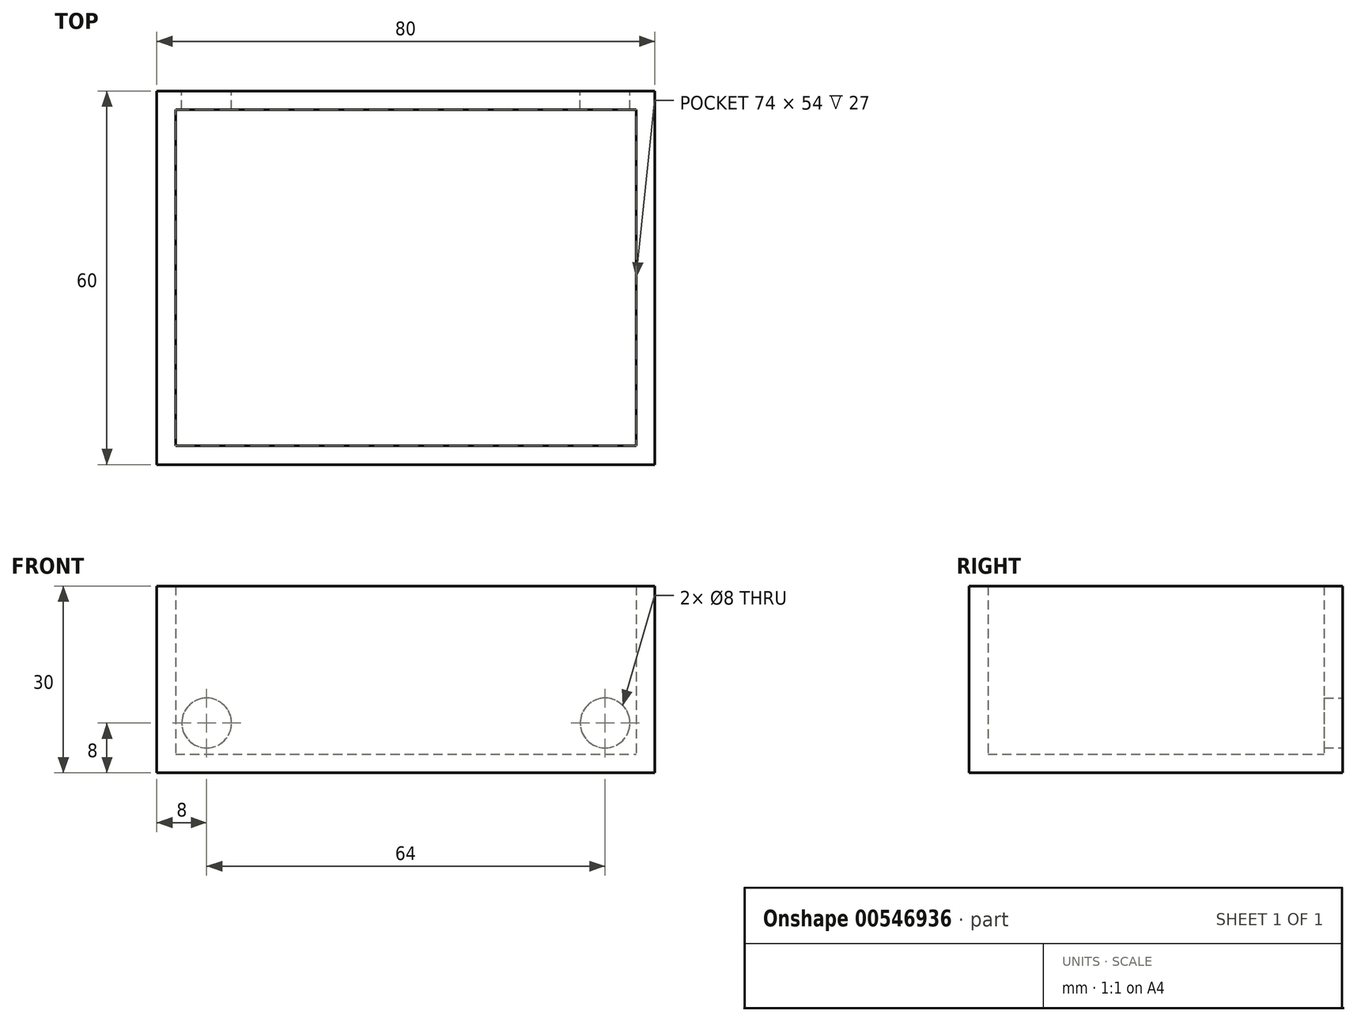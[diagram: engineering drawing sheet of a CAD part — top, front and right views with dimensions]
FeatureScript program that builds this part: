
annotation { "Feature Type Name" : "Feature", "Feature Type Description" : "" }
export const myFeature = defineFeature(function(context is Context, id is Id, definition is map)
    precondition{}
    {
        {
            var Q0;
            Q0=qCreatedBy(makeId("Top.planeOp"),FACE);
            var sketch = newSketch(context, id + "F0", { "sketchPlane" : qUnion([Q0])});
            skLineSegment(sketch, "E0.bottom", {"start": v(0, 0) * mm, "end": v(80, 0) * mm});
            skLineSegment(sketch, "E0.top", {"start": v(0, -60) * mm, "end": v(80, -60) * mm});
            skLineSegment(sketch, "E0.left", {"start": v(0, 0) * mm, "end": v(0, -60) * mm});
            skLineSegment(sketch, "E0.right", {"start": v(80, 0) * mm, "end": v(80, -60) * mm});
            skLineSegment(sketch, "E1", {"start": v(0, 0) * mm, "end": v(0, -3) * mm, "construction": true});
            skLineSegment(sketch, "E2", {"start": v(0, -3) * mm, "end": v(3, -3) * mm, "construction": true});
            skLineSegment(sketch, "E3", {"start": v(3, -3) * mm, "end": v(77, -3) * mm});
            skLineSegment(sketch, "E4", {"start": v(77, -3) * mm, "end": v(77, -57) * mm});
            skLineSegment(sketch, "E5", {"start": v(77, -57) * mm, "end": v(3, -57) * mm});
            skLineSegment(sketch, "E6", {"start": v(3, -57) * mm, "end": v(3, -3) * mm});
            skSolve(sketch);
        }
        {
            var Q0;
            Q0=makeQuery(id+"F0.imprint","IMPRINT",FACE,{"disambiguationData":[TD([[makeQuery(id+"F0.imprint","IMPRINT",EDGE,{"derivedFrom":sQuery(id+"F0.wireOp",EDGE,"E3")}),-1.0]])]});
            extrude(context, id + "F1", {"entities" : qUnion([Q0]), "depth" : 3 * mm, "offsetDistance" : 25 * mm});
        }
        {
            var Q0;
            Q0=makeQuery(id+"F0.imprint","IMPRINT",FACE,{"disambiguationData":[TD([[makeQuery(id+"F0.imprint","IMPRINT",EDGE,{"derivedFrom":sQuery(id+"F0.wireOp",EDGE,"E0.bottom")}),-1.0]])]});
            extrude(context, id + "F2", {"entities" : qUnion([Q0]), "operationType" : NewBodyOperationType.ADD, "depth" : 30 * mm, "offsetDistance" : 25 * mm});
        }
        {
            var Q0;
            Q0=qCreatedBy(makeId("Front.planeOp"),FACE);
            var sketch = newSketch(context, id + "F3", { "sketchPlane" : qUnion([Q0])});
            skLineSegment(sketch, "E7", {"start": v(0, 0) * mm, "end": v(80, 0) * mm, "construction": true});
            skLineSegment(sketch, "E8.0", {"start": v(0, 8) * mm, "end": v(80, 8) * mm, "construction": true});
            skLineSegment(sketch, "E9", {"start": v(80, 0) * mm, "end": v(80, 8) * mm, "construction": true});
            skLineSegment(sketch, "E10", {"start": v(0, 0) * mm, "end": v(0, 8) * mm, "construction": true});
            skLineSegment(sketch, "E11.0", {"start": v(72, 0) * mm, "end": v(72, 8) * mm, "construction": true});
            skLineSegment(sketch, "E12.0", {"start": v(8, 0) * mm, "end": v(8, 8) * mm, "construction": true});
            skCircle(sketch, "E13", {"center": v(72, 8) * mm, "radius": 4 * mm});
            skCircle(sketch, "E14", {"center": v(8, 8) * mm, "radius": 4 * mm});
            skSolve(sketch);
        }
        {
            var Q0;
            Q0=makeQuery(id+"F3.imprint","IMPRINT",FACE,{"disambiguationData":[TD([[makeQuery(id+"F3.imprint","IMPRINT",EDGE,{"derivedFrom":sQuery(id+"F3.wireOp",EDGE,"E13")}),1.0]])]});
            var Q1;
            Q1=makeQuery(id+"F3.imprint","IMPRINT",FACE,{"disambiguationData":[TD([[makeQuery(id+"F3.imprint","IMPRINT",EDGE,{"derivedFrom":sQuery(id+"F3.wireOp",EDGE,"E14")}),1.0]])]});
            extrude(context, id + "F4", {"entities" : qUnion([Q0, Q1]), "operationType" : NewBodyOperationType.REMOVE, "depth" : 5 * mm, "offsetDistance" : 25 * mm});
        }
    });
